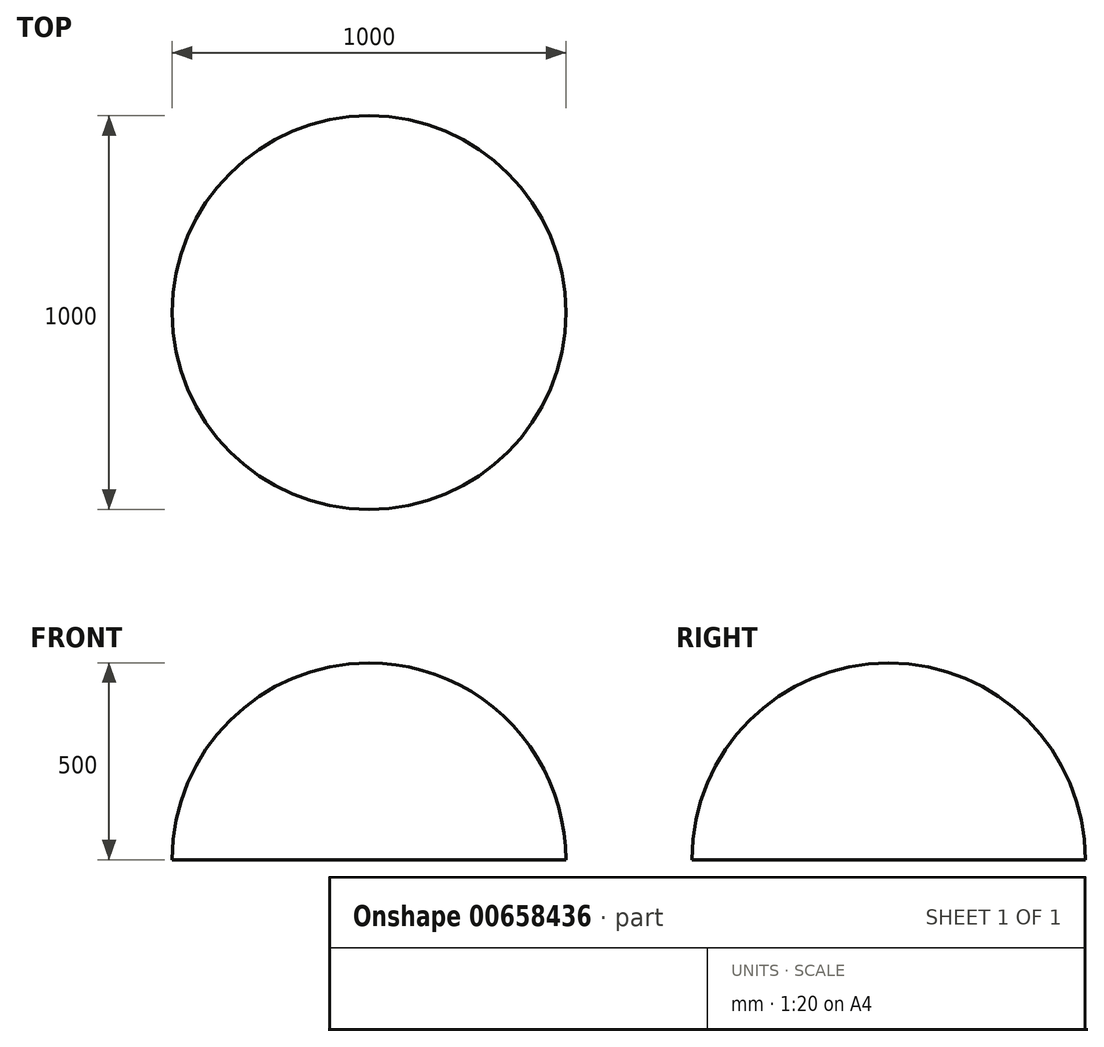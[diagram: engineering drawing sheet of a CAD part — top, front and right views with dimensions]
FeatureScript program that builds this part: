
annotation { "Feature Type Name" : "Feature", "Feature Type Description" : "" }
export const myFeature = defineFeature(function(context is Context, id is Id, definition is map)
    precondition{}
    {
        {
            var Q0;
            Q0=qCreatedBy(makeId("Front.planeOp"),FACE);
            var sketch = newSketch(context, id + "F0", { "sketchPlane" : qUnion([Q0])});
            skArc(sketch, "E0", {"start": v(500, 0) * mm, "mid": v(353.55, 353.55) * mm, "end": v(0, 500) * mm});
            skLineSegment(sketch, "E1", {"start": v(0, 0) * mm, "end": v(500, 0) * mm});
            skPoint(sketch, "E2.orphan", {"position": v(-500, 0) * mm});
            skLineSegment(sketch, "E3", {"start": v(0, 500) * mm, "end": v(0, 0) * mm});
            skSolve(sketch);
        }
        {
            var Q0;
            Q0=makeQuery(id+"F0.imprint","IMPRINT",FACE,{"disambiguationData":[TD([[makeQuery(id+"F0.imprint","IMPRINT",EDGE,{"derivedFrom":sQuery(id+"F0.wireOp",EDGE,"E0")}),1.0]])]});
            var Q1;
            Q1=sQuery(id+"F0.wireOp",EDGE,"E3");
            revolve(context, id + "F1", {"entities" : qUnion([Q0]), "axis" : qUnion([Q1]), "revolveType" : RevolveType.FULL});
        }
    });
